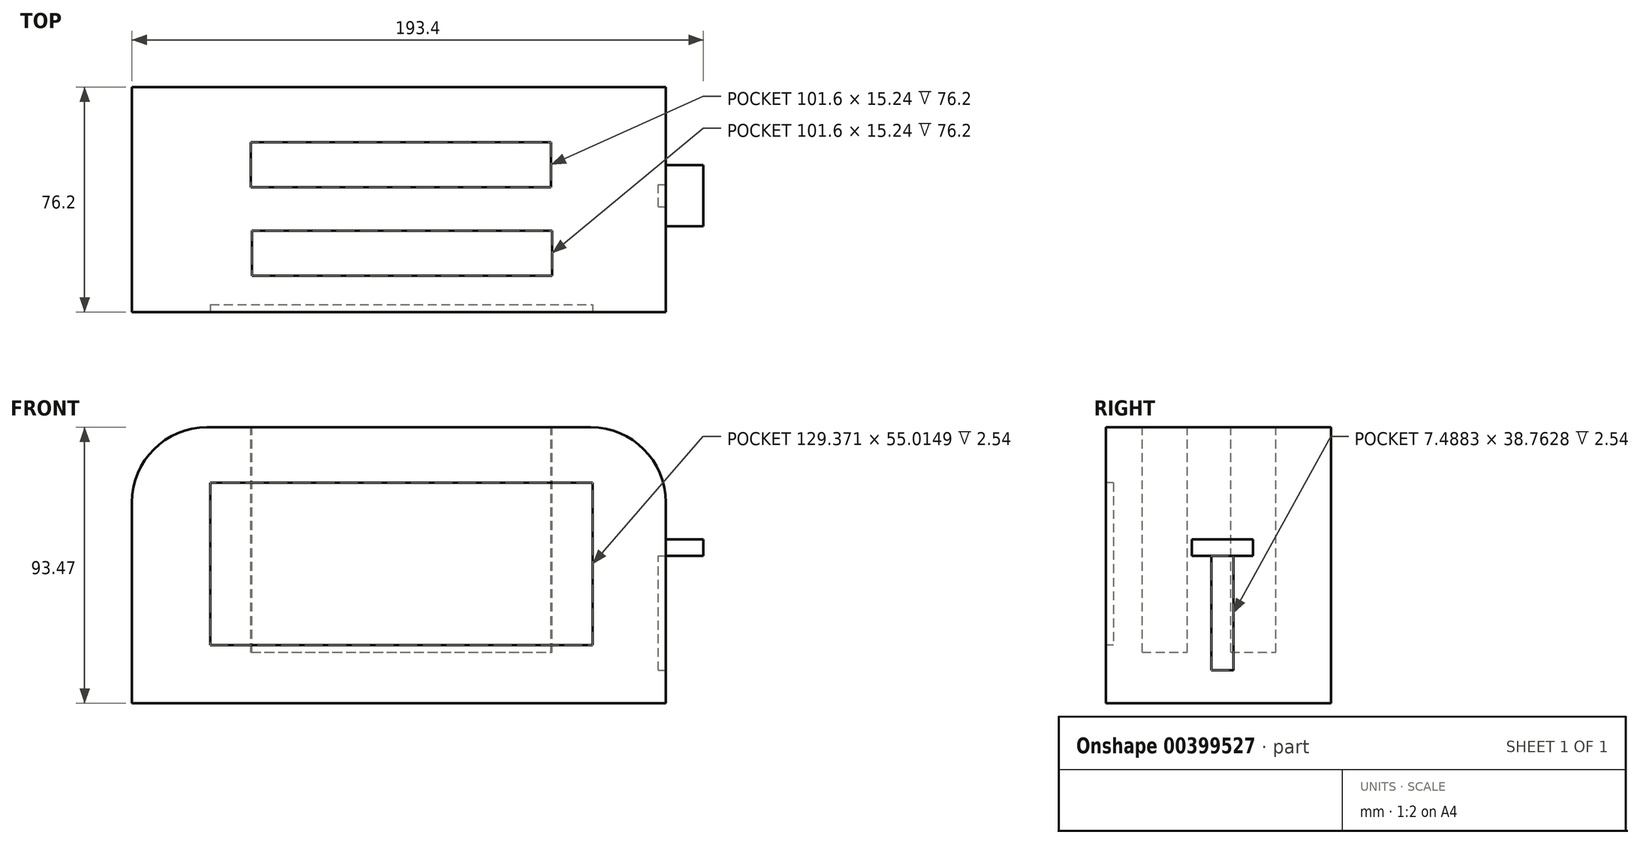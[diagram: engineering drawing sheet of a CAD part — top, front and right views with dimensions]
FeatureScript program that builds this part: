
annotation { "Feature Type Name" : "Feature", "Feature Type Description" : "" }
export const myFeature = defineFeature(function(context is Context, id is Id, definition is map)
    precondition{}
    {
        {
            var Q0;
            Q0=qCreatedBy(makeId("Front.planeOp"),FACE);
            var sketch = newSketch(context, id + "F0", { "sketchPlane" : qUnion([Q0])});
            skLineSegment(sketch, "E0.bottom", {"start": v(-90.35, 37.97) * mm, "end": v(90.35, 37.97) * mm});
            skLineSegment(sketch, "E0.top", {"start": v(-90.35, -55.5) * mm, "end": v(90.35, -55.5) * mm});
            skLineSegment(sketch, "E0.left", {"start": v(-90.35, 37.97) * mm, "end": v(-90.35, -55.5) * mm});
            skLineSegment(sketch, "E0.right", {"start": v(90.35, 37.97) * mm, "end": v(90.35, -55.5) * mm});
            skSolve(sketch);
        }
        {
            var Q0;
            Q0=makeQuery(id+"F0.imprint","IMPRINT",FACE,{"disambiguationData":[TD([[makeQuery(id+"F0.imprint","IMPRINT",EDGE,{"derivedFrom":sQuery(id+"F0.wireOp",EDGE,"E0.bottom")}),-1.0]])]});
            extrude(context, id + "F1", {"entities" : qUnion([Q0]), "depth" : 76.2 * mm});
        }
        {
            var Q0;
            Q0=makeQuery(id+"F1.opExtrude","SWEPT_EDGE",EDGE,{"disambiguationData":[OSD([sQuery(id+"F0.wireOp",EDGE,"E0.bottom"),sQuery(id+"F0.wireOp",EDGE,"E0.right")])]});
            var Q1;
            Q1=makeQuery(id+"F1.opExtrude","SWEPT_EDGE",EDGE,{"disambiguationData":[OSD([sQuery(id+"F0.wireOp",EDGE,"E0.bottom"),sQuery(id+"F0.wireOp",EDGE,"E0.left")])]});
            fillet(context, id + "F2", {"entities" : qUnion([Q0, Q1]), "radius" : 25.4 * mm, "tangentPropagation" : true, "allowEdgeOverflow" : false});
        }
        {
            var Q0;
            Q0=makeQuery(id+"F1.opExtrude","SWEPT_FACE",FACE,{"disambiguationData":[OSD([sQuery(id+"F0.wireOp",EDGE,"E0.bottom")])]});
            var sketch = newSketch(context, id + "F3", { "sketchPlane" : qUnion([Q0])});
            skLineSegment(sketch, "E1.bottom", {"start": v(-49.71, -63.9) * mm, "end": v(51.89, -63.9) * mm});
            skLineSegment(sketch, "E1.top", {"start": v(-49.71, -48.65) * mm, "end": v(51.89, -48.65) * mm});
            skLineSegment(sketch, "E1.left", {"start": v(-49.71, -63.9) * mm, "end": v(-49.71, -48.65) * mm});
            skLineSegment(sketch, "E1.right", {"start": v(51.89, -63.9) * mm, "end": v(51.89, -48.65) * mm});
            skLineSegment(sketch, "E2.bottom", {"start": v(-50.12, -33.94) * mm, "end": v(51.48, -33.94) * mm});
            skLineSegment(sketch, "E2.top", {"start": v(-50.12, -18.7) * mm, "end": v(51.48, -18.7) * mm});
            skLineSegment(sketch, "E2.left", {"start": v(-50.12, -33.94) * mm, "end": v(-50.12, -18.7) * mm});
            skLineSegment(sketch, "E2.right", {"start": v(51.48, -33.94) * mm, "end": v(51.48, -18.7) * mm});
            skSolve(sketch);
        }
        {
            var Q0;
            Q0=makeQuery(id+"F3.imprint","IMPRINT",FACE,{"disambiguationData":[TD([[makeQuery(id+"F3.imprint","IMPRINT",EDGE,{"derivedFrom":sQuery(id+"F3.wireOp",EDGE,"E1.bottom")}),1.0]])]});
            var Q1;
            Q1=makeQuery(id+"F3.imprint","IMPRINT",FACE,{"disambiguationData":[TD([[makeQuery(id+"F3.imprint","IMPRINT",EDGE,{"derivedFrom":sQuery(id+"F3.wireOp",EDGE,"E2.bottom")}),1.0]])]});
            extrude(context, id + "F4", {"entities" : qUnion([Q0, Q1]), "operationType" : NewBodyOperationType.REMOVE, "oppositeDirection" : true, "depth" : 76.2 * mm});
        }
        {
            var Q0;
            Q0=makeQuery(id+"F1.opExtrude","CAP_FACE",FACE,{"disambiguationData":[OSD([sQuery(id+"F0.wireOp",EDGE,"E0.bottom"),sQuery(id+"F0.wireOp",EDGE,"E0.top"),sQuery(id+"F0.wireOp",EDGE,"E0.left"),sQuery(id+"F0.wireOp",EDGE,"E0.right")])],"isStart":false});
            var sketch = newSketch(context, id + "F5", { "sketchPlane" : qUnion([Q0])});
            skLineSegment(sketch, "E3.bottom", {"start": v(-63.83, 19.17) * mm, "end": v(65.55, 19.17) * mm});
            skLineSegment(sketch, "E3.top", {"start": v(-63.83, -35.84) * mm, "end": v(65.55, -35.84) * mm});
            skLineSegment(sketch, "E3.left", {"start": v(-63.83, 19.17) * mm, "end": v(-63.83, -35.84) * mm});
            skLineSegment(sketch, "E3.right", {"start": v(65.55, 19.17) * mm, "end": v(65.55, -35.84) * mm});
            skSolve(sketch);
        }
        {
            var Q0;
            Q0=makeQuery(id+"F5.imprint","IMPRINT",FACE,{"disambiguationData":[TD([[makeQuery(id+"F5.imprint","IMPRINT",EDGE,{"derivedFrom":sQuery(id+"F5.wireOp",EDGE,"E3.bottom")}),-1.0]])]});
            extrude(context, id + "F6", {"entities" : qUnion([Q0]), "operationType" : NewBodyOperationType.REMOVE, "oppositeDirection" : true, "depth" : 2.54 * mm});
        }
        {
            var Q0;
            Q0=makeQuery(id+"F1.opExtrude","SWEPT_FACE",FACE,{"disambiguationData":[OSD([sQuery(id+"F0.wireOp",EDGE,"E0.right")])]});
            var sketch = newSketch(context, id + "F7", { "sketchPlane" : qUnion([Q0])});
            skLineSegment(sketch, "E4.bottom", {"start": v(-47.13, 0) * mm, "end": v(-26.43, 0) * mm});
            skLineSegment(sketch, "E4.top", {"start": v(-47.13, -5.6) * mm, "end": v(-26.43, -5.6) * mm});
            skLineSegment(sketch, "E4.left", {"start": v(-47.13, 0) * mm, "end": v(-47.13, -5.6) * mm});
            skLineSegment(sketch, "E4.right", {"start": v(-26.43, 0) * mm, "end": v(-26.43, -5.6) * mm});
            skSolve(sketch);
        }
        {
            var Q0;
            Q0=makeQuery(id+"F7.imprint","IMPRINT",FACE,{"disambiguationData":[TD([[makeQuery(id+"F7.imprint","IMPRINT",EDGE,{"derivedFrom":sQuery(id+"F7.wireOp",EDGE,"E4.bottom")}),-1.0]])]});
            extrude(context, id + "F8", {"entities" : qUnion([Q0]), "operationType" : NewBodyOperationType.ADD, "depth" : 12.7 * mm});
        }
        {
            var Q0;
            Q0=makeQuery(id+"F1.opExtrude","SWEPT_FACE",FACE,{"disambiguationData":[OSD([sQuery(id+"F0.wireOp",EDGE,"E0.right")])]});
            var sketch = newSketch(context, id + "F9", { "sketchPlane" : qUnion([Q0])});
            skLineSegment(sketch, "E5.bottom", {"start": v(-40.52, -44.37) * mm, "end": v(-33.03, -44.37) * mm});
            skLineSegment(sketch, "E5.top", {"start": v(-40.52, -5.6) * mm, "end": v(-33.03, -5.6) * mm});
            skLineSegment(sketch, "E5.left", {"start": v(-40.52, -44.37) * mm, "end": v(-40.52, -5.6) * mm});
            skLineSegment(sketch, "E5.right", {"start": v(-33.03, -44.37) * mm, "end": v(-33.03, -5.6) * mm});
            skPoint(sketch, "E5.middle", {"position": v(-36.78, -24.99) * mm});
            skPoint(sketch, "E5.middle.positionSnap0", {"position": v(-36.78, -5.6) * mm});
            skPoint(sketch, "E5.centerSnap0", {"position": v(-36.78, -5.6) * mm});
            skSolve(sketch);
        }
        {
            var Q0;
            Q0=makeQuery(id+"F9.imprint","IMPRINT",FACE,{"disambiguationData":[TD([[makeQuery(id+"F9.imprint","IMPRINT",EDGE,{"derivedFrom":sQuery(id+"F9.wireOp",EDGE,"E5.bottom")}),1.0]])]});
            extrude(context, id + "F10", {"entities" : qUnion([Q0]), "operationType" : NewBodyOperationType.REMOVE, "oppositeDirection" : true, "depth" : 2.54 * mm});
        }
    });
